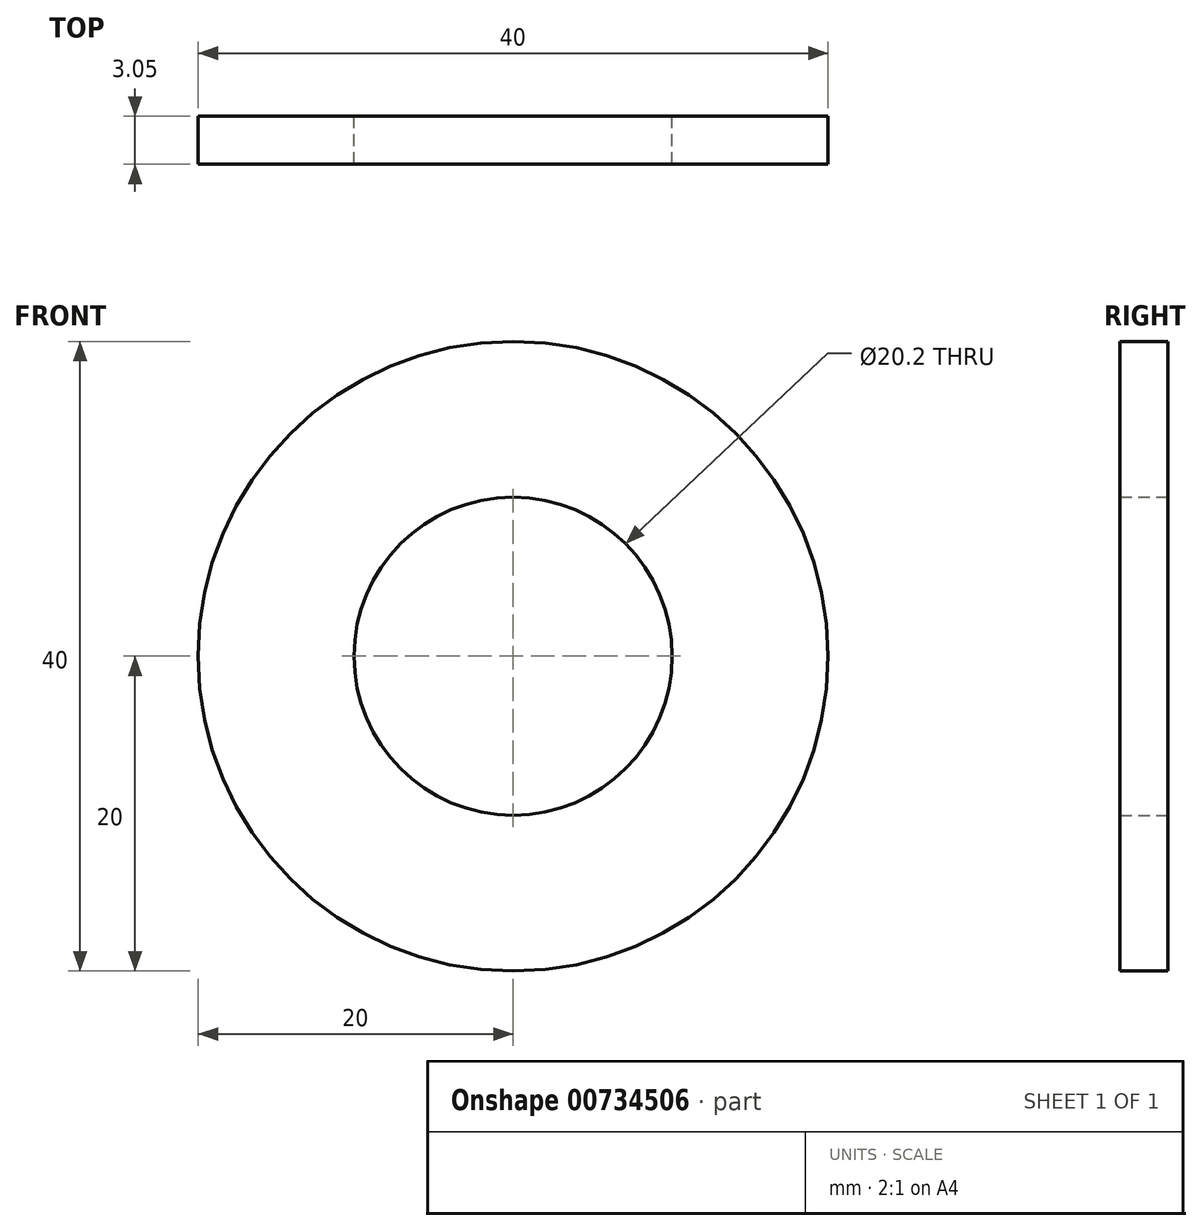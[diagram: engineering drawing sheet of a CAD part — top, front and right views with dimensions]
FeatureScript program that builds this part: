
annotation { "Feature Type Name" : "Feature", "Feature Type Description" : "" }
export const myFeature = defineFeature(function(context is Context, id is Id, definition is map)
    precondition{}
    {
        {
            var Q0;
            Q0=qCreatedBy(makeId("Front.planeOp"),FACE);
            var sketch = newSketch(context, id + "F0", { "sketchPlane" : qUnion([Q0])});
            skCircle(sketch, "E0", {"center": v(0, 0) * mm, "radius": 20 * mm});
            skCircle(sketch, "E1", {"center": v(0, 0) * mm, "radius": 10.1 * mm});
            skSolve(sketch);
        }
        {
            var Q0;
            Q0 = qSketchRegion(id + "F0", true);
            extrude(context, id + "F1", {"entities" : qUnion([Q0]), "depth" : 3.05 * mm, "offsetDistance" : 25.4 * mm});
        }
    });
